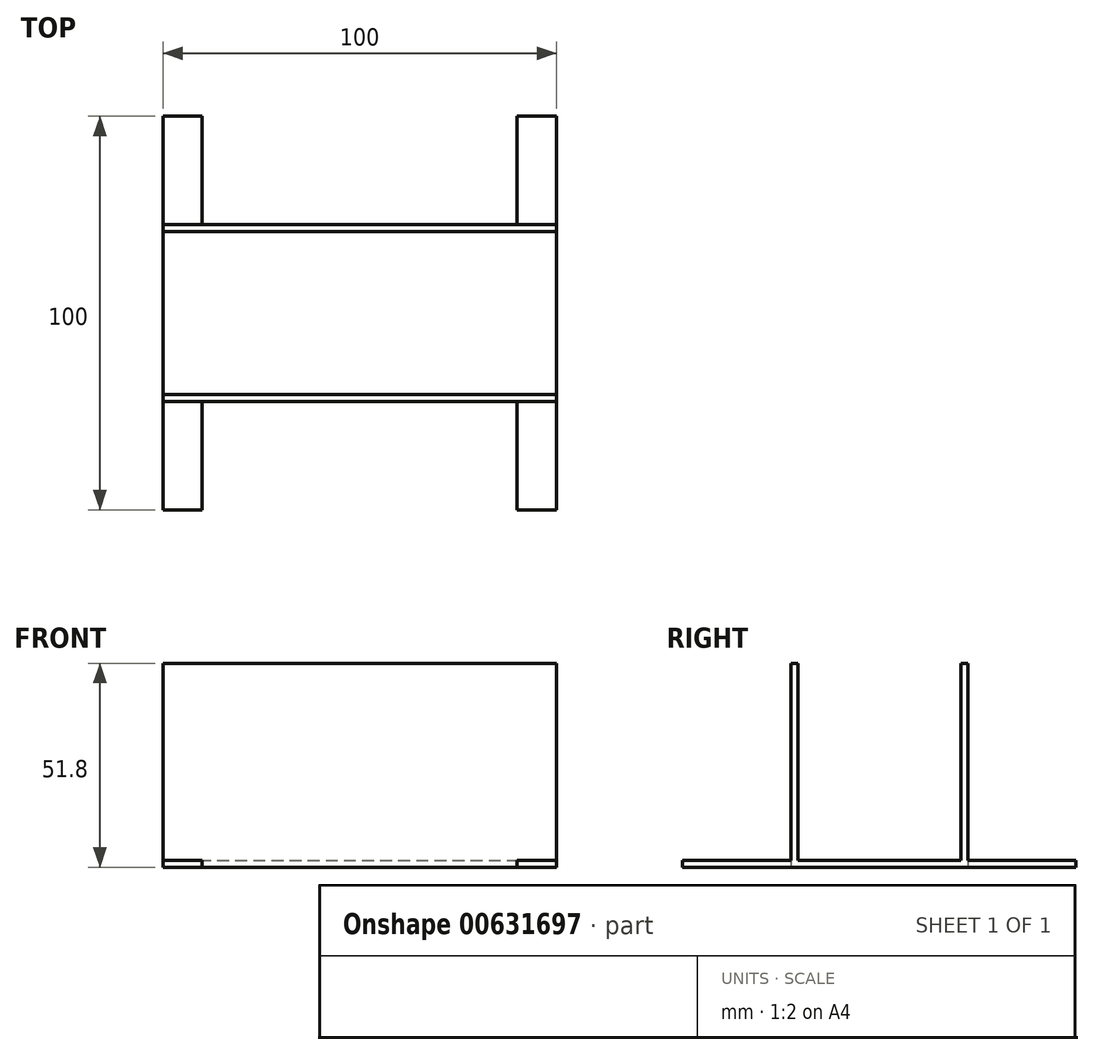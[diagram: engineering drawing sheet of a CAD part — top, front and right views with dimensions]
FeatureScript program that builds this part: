
annotation { "Feature Type Name" : "Feature", "Feature Type Description" : "" }
export const myFeature = defineFeature(function(context is Context, id is Id, definition is map)
    precondition{}
    {
        {
            var Q0;
            Q0=qCreatedBy(makeId("Top.planeOp"),FACE);
            var sketch = newSketch(context, id + "F0", { "sketchPlane" : qUnion([Q0])});
            skLineSegment(sketch, "E0.bottom", {"start": v(-50, 22.5) * mm, "end": v(50, 22.5) * mm});
            skLineSegment(sketch, "E0.top", {"start": v(-50, -22.5) * mm, "end": v(50, -22.5) * mm});
            skLineSegment(sketch, "E0.left", {"start": v(-50, 22.5) * mm, "end": v(-50, -22.5) * mm});
            skLineSegment(sketch, "E0.right", {"start": v(50, 22.5) * mm, "end": v(50, -22.5) * mm});
            skPoint(sketch, "E0.middle", {"position": v(0, 0) * mm});
            skSolve(sketch);
        }
        {
            var Q0;
            Q0=makeQuery(id+"F0.imprint","IMPRINT",FACE,{"disambiguationData":[TD([[makeQuery(id+"F0.imprint","IMPRINT",EDGE,{"derivedFrom":sQuery(id+"F0.wireOp",EDGE,"E0.bottom")}),-1.0]])]});
            extrude(context, id + "F1", {"entities" : qUnion([Q0]), "depth" : 50 * mm, "offsetDistance" : 25 * mm, "hasSecondDirection" : true, "secondDirectionOppositeDirection" : true, "secondDirectionDepth" : 1.8 * mm});
        }
        {
            var Q0;
            Q0=makeQuery(id+"F1.opExtrude","CAP_FACE",FACE,{"disambiguationData":[OSD([sQuery(id+"F0.wireOp",EDGE,"E0.bottom"),sQuery(id+"F0.wireOp",EDGE,"E0.top"),sQuery(id+"F0.wireOp",EDGE,"E0.left"),sQuery(id+"F0.wireOp",EDGE,"E0.right")])],"isStart":false});
            var Q1;
            Q1=makeQuery(id+"F1.opExtrude","SWEPT_FACE",FACE,{"disambiguationData":[OSD([sQuery(id+"F0.wireOp",EDGE,"E0.left")])]});
            var Q2;
            Q2=makeQuery(id+"F1.opExtrude","SWEPT_FACE",FACE,{"disambiguationData":[OSD([sQuery(id+"F0.wireOp",EDGE,"E0.right")])]});
            shell(context, id + "F2", {"entities" : qUnion([Q0, Q1, Q2]), "thickness" : 1.8 * mm});
        }
        {
            var Q0;
            Q0=qCreatedBy(makeId("Top.planeOp"),FACE);
            var sketch = newSketch(context, id + "F3", { "sketchPlane" : qUnion([Q0])});
            skLineSegment(sketch, "E1", {"start": v(0, 0) * mm, "end": v(-45, 0) * mm});
            skLineSegment(sketch, "E2", {"start": v(0, 0) * mm, "end": v(45, 0) * mm});
            skLineSegment(sketch, "E3.bottom", {"start": v(-50, -50) * mm, "end": v(-40, -50) * mm});
            skLineSegment(sketch, "E3.top", {"start": v(-50, 50) * mm, "end": v(-40, 50) * mm});
            skLineSegment(sketch, "E3.left", {"start": v(-50, -50) * mm, "end": v(-50, 50) * mm});
            skLineSegment(sketch, "E3.right", {"start": v(-40, -50) * mm, "end": v(-40, 50) * mm});
            skPoint(sketch, "E3.middle", {"position": v(-45, 0) * mm});
            skLineSegment(sketch, "E4.bottom", {"start": v(50, -50) * mm, "end": v(40, -50) * mm});
            skLineSegment(sketch, "E4.top", {"start": v(50, 50) * mm, "end": v(40, 50) * mm});
            skLineSegment(sketch, "E4.left", {"start": v(50, -50) * mm, "end": v(50, 50) * mm});
            skLineSegment(sketch, "E4.right", {"start": v(40, -50) * mm, "end": v(40, 50) * mm});
            skPoint(sketch, "E4.middle", {"position": v(45, 0) * mm});
            skSolve(sketch);
        }
        {
            var Q0;
            {var subQ0=sQuery(id+"F3.wireOp",EDGE,"E3.bottom");Q0=makeQuery(id+"F3.imprint","IMPRINT",FACE,{"disambiguationData":[TD([[makeQuery(id+"F3.imprint","IMPRINT",EDGE,{"derivedFrom":subQ0}),1.0]])]});}
            var Q1;
            {var subQ1=sQuery(id+"F3.wireOp",EDGE,"E4.bottom");Q1=makeQuery(id+"F3.imprint","IMPRINT",FACE,{"disambiguationData":[TD([[makeQuery(id+"F3.imprint","IMPRINT",EDGE,{"derivedFrom":subQ1}),-1.0]])]});}
            extrude(context, id + "F4", {"entities" : qUnion([Q0, Q1]), "operationType" : NewBodyOperationType.ADD, "oppositeDirection" : true, "depth" : 1.8 * mm, "offsetDistance" : 25 * mm});
        }
    });
